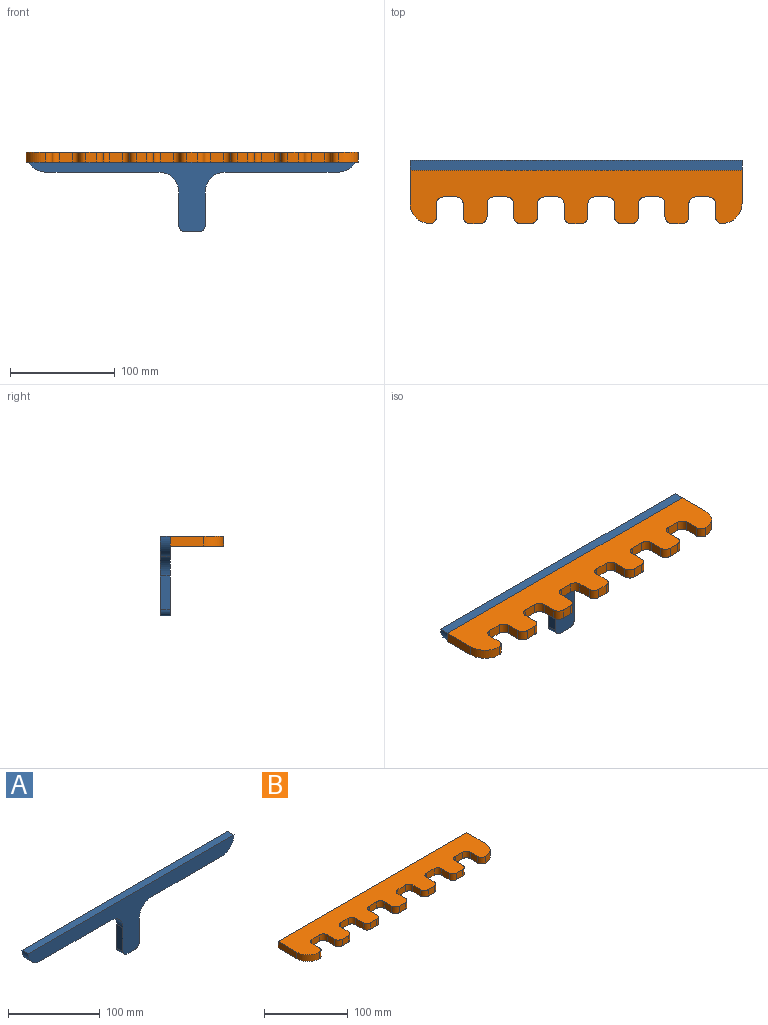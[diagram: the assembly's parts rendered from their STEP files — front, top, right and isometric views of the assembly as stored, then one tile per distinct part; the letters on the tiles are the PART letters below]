
ASSEMBLY  parts=2 mates=1
PART A: 14 faces, bbox 317.5x9.5x76.2 mm
  f0: plane 12.7x9.53mm, normal (0,0,-1), area 121mm2, adj f1,f11,f12,f13
  f1: cylinder r=6.35mm len=9.53mm, axis (0,1,0), area 95mm2, adj f0,f2,f12,f13
  f2: plane 31.75x9.53mm, normal (1,0,0), area 302.4mm2, adj f1,f3,f12,f13
  f3: cylinder r=19.05mm len=19.05mm, axis (0,1,0), area 285mm2, adj f2,f4,f12,f13
  f4: plane 107.95x9.53mm, normal (0,0,-1), area 1028.2mm2, adj f3,f5,f12,f13
  f5: cylinder r=19.05mm len=19.05mm, axis (0,1,0), area 285mm2, adj f4,f6,f12,f13
  f6: plane 317.5x9.53mm, normal (0,0,1), area 3024.2mm2, adj f5,f7,f12,f13
  f7: cylinder r=19.05mm len=19.05mm, axis (0,1,0), area 285mm2, adj f6,f8,f12,f13
  f8: plane 107.95x9.53mm, normal (0,0,-1), area 1028.2mm2, adj f7,f9,f12,f13
  f9: cylinder r=19.05mm len=19.05mm, axis (0,1,0), area 285mm2, adj f8,f10,f12,f13
  f10: plane 31.75x9.53mm, normal (-1,0,0), area 302.4mm2, adj f9,f11,f12,f13
  f11: cylinder r=6.35mm len=9.53mm, axis (0,1,0), area 95mm2, adj f0,f10,f12,f13
  f12: plane 317.5x76.2mm, normal (0,-1,0), area 7482.7mm2, adj f0,f1,f2,f3,f4,f5,f6,f7
  f13: plane 317.5x76.2mm, normal (0,1,0), area 7482.7mm2, adj f0,f1,f2,f3,f4,f5,f6,f7
PART B: 54 faces, bbox 317.5x50.8x9.5 mm
  f0: cylinder r=6.35mm len=9.53mm, axis (0,0,-1), area 95mm2, adj f1,f51,f52,f53
  f1: plane 12.7x9.53mm, normal (0,-1,0), area 121mm2, adj f0,f2,f52,f53
  f2: cylinder r=6.35mm len=9.53mm, axis (0,0,-1), area 95mm2, adj f1,f3,f52,f53
  f3: plane 12.7x9.53mm, normal (-1,0,0), area 121mm2, adj f2,f4,f52,f53
  f4: cylinder r=6.35mm len=9.53mm, axis (0,0,-1), area 95mm2, adj f3,f5,f52,f53
  f5: plane 10.16x9.53mm, normal (0,-1,0), area 96.8mm2, adj f4,f6,f52,f53
  f6: cylinder r=6.35mm len=9.53mm, axis (0,0,-1), area 95mm2, adj f5,f7,f52,f53
  f7: plane 12.7x9.53mm, normal (1,0,0), area 121mm2, adj f6,f8,f52,f53
  f8: cylinder r=6.35mm len=9.53mm, axis (0,0,-1), area 95mm2, adj f7,f9,f52,f53
  f9: plane 12.7x9.53mm, normal (0,-1,0), area 121mm2, adj f8,f10,f52,f53
  f10: cylinder r=6.35mm len=9.53mm, axis (0,0,-1), area 95mm2, adj f9,f11,f52,f53
  f11: plane 12.7x9.53mm, normal (-1,0,0), area 121mm2, adj f10,f12,f52,f53
  f12: cylinder r=6.35mm len=9.53mm, axis (0,0,-1), area 95mm2, adj f11,f13,f52,f53
  f13: plane 10.16x9.53mm, normal (0,-1,0), area 96.8mm2, adj f12,f14,f52,f53
  f14: cylinder r=6.35mm len=9.53mm, axis (0,0,-1), area 95mm2, adj f13,f15,f52,f53
  f15: plane 12.7x9.53mm, normal (1,0,0), area 121mm2, adj f14,f16,f52,f53
  f16: cylinder r=6.35mm len=9.53mm, axis (0,0,-1), area 95mm2, adj f15,f17,f52,f53
  f17: plane 12.7x9.53mm, normal (0,-1,0), area 121mm2, adj f16,f18,f52,f53
  f18: cylinder r=6.35mm len=9.53mm, axis (0,0,-1), area 95mm2, adj f17,f19,f52,f53
  f19: plane 12.7x9.53mm, normal (-1,0,0), area 121mm2, adj f18,f20,f52,f53
  f20: cylinder r=6.35mm len=9.53mm, axis (0,0,-1), area 95mm2, adj f19,f21,f52,f53
  f21: plane 10.16x9.53mm, normal (0,-1,0), area 96.8mm2, adj f20,f22,f52,f53
  f22: cylinder r=6.35mm len=9.53mm, axis (0,0,-1), area 95mm2, adj f21,f23,f52,f53
  f23: plane 12.7x9.53mm, normal (1,0,0), area 121mm2, adj f22,f24,f52,f53
  f24: cylinder r=6.35mm len=9.53mm, axis (0,0,-1), area 95mm2, adj f23,f25,f52,f53
  f25: plane 12.7x9.53mm, normal (0,-1,0), area 121mm2, adj f24,f26,f52,f53
  f26: cylinder r=6.35mm len=9.53mm, axis (0,0,-1), area 95mm2, adj f25,f27,f52,f53
  f27: plane 12.7x9.53mm, normal (-1,0,0), area 121mm2, adj f26,f28,f52,f53
  f28: cylinder r=6.35mm len=9.53mm, axis (0,0,-1), area 95mm2, adj f27,f29,f52,f53
  f29: plane 10.16x9.53mm, normal (0,-1,0), area 96.8mm2, adj f28,f30,f52,f53
  f30: cylinder r=6.35mm len=9.53mm, axis (0,0,-1), area 95mm2, adj f29,f31,f52,f53
  f31: plane 12.7x9.53mm, normal (1,0,0), area 121mm2, adj f30,f32,f52,f53
  f32: cylinder r=6.35mm len=9.53mm, axis (0,0,-1), area 95mm2, adj f31,f33,f52,f53
  f33: plane 12.7x9.53mm, normal (0,-1,0), area 121mm2, adj f32,f34,f52,f53
  f34: cylinder r=6.35mm len=9.53mm, axis (0,0,-1), area 95mm2, adj f33,f35,f52,f53
  f35: plane 12.7x9.53mm, normal (-1,0,0), area 121mm2, adj f34,f36,f52,f53
  f36: cylinder r=6.35mm len=9.53mm, axis (0,0,-1), area 95mm2, adj f35,f37,f52,f53
  f37: plane 10.16x9.53mm, normal (0,-1,0), area 96.8mm2, adj f36,f38,f52,f53
  f38: cylinder r=6.35mm len=9.53mm, axis (0,0,-1), area 95mm2, adj f37,f39,f52,f53
  f39: plane 12.7x9.53mm, normal (1,0,0), area 121mm2, adj f38,f40,f52,f53
  f40: cylinder r=6.35mm len=9.53mm, axis (0,0,-1), area 95mm2, adj f39,f41,f52,f53
  f41: plane 12.7x9.53mm, normal (0,-1,0), area 121mm2, adj f40,f42,f52,f53
  f42: cylinder r=6.35mm len=9.53mm, axis (0,0,-1), area 95mm2, adj f41,f43,f52,f53
  f43: plane 12.7x9.53mm, normal (-1,0,0), area 121mm2, adj f42,f44,f52,f53
  f44: cylinder r=6.35mm len=9.53mm, axis (0,0,-1), area 95mm2, adj f43,f45,f52,f53
  f45: cylinder r=19.05mm len=19.05mm, axis (0,0,-1), area 285mm2, adj f44,f46,f52,f53
  f46: plane 31.75x9.53mm, normal (1,0,0), area 302.4mm2, adj f45,f47,f52,f53
  f47: plane 317.5x9.53mm, normal (0,1,0), area 3024.2mm2, adj f46,f48,f52,f53
  f48: plane 31.75x9.53mm, normal (-1,0,0), area 302.4mm2, adj f47,f49,f52,f53
  f49: cylinder r=19.05mm len=19.05mm, axis (0,0,-1), area 285mm2, adj f48,f50,f52,f53
  f50: cylinder r=6.35mm len=9.53mm, axis (0,0,-1), area 95mm2, adj f49,f51,f52,f53
  f51: plane 12.7x9.53mm, normal (1,0,0), area 121mm2, adj f0,f50,f52,f53
  f52: plane 317.5x50.8mm, normal (0,0,1), area 12102.3mm2, adj f0,f1,f2,f3,f4,f5,f6,f7
  f53: plane 317.5x50.8mm, normal (0,0,-1), area 12102.3mm2, adj f0,f1,f2,f3,f4,f5,f6,f7
PLACE A t=(-152.08,25.4,-38.1)mm
PLACE B t=(-152.08,-9.53,-9.53)mm
MATE fastened B.f47 <-> A.f12  axis (0,1,0) through (6.67,15.88,0)mm
